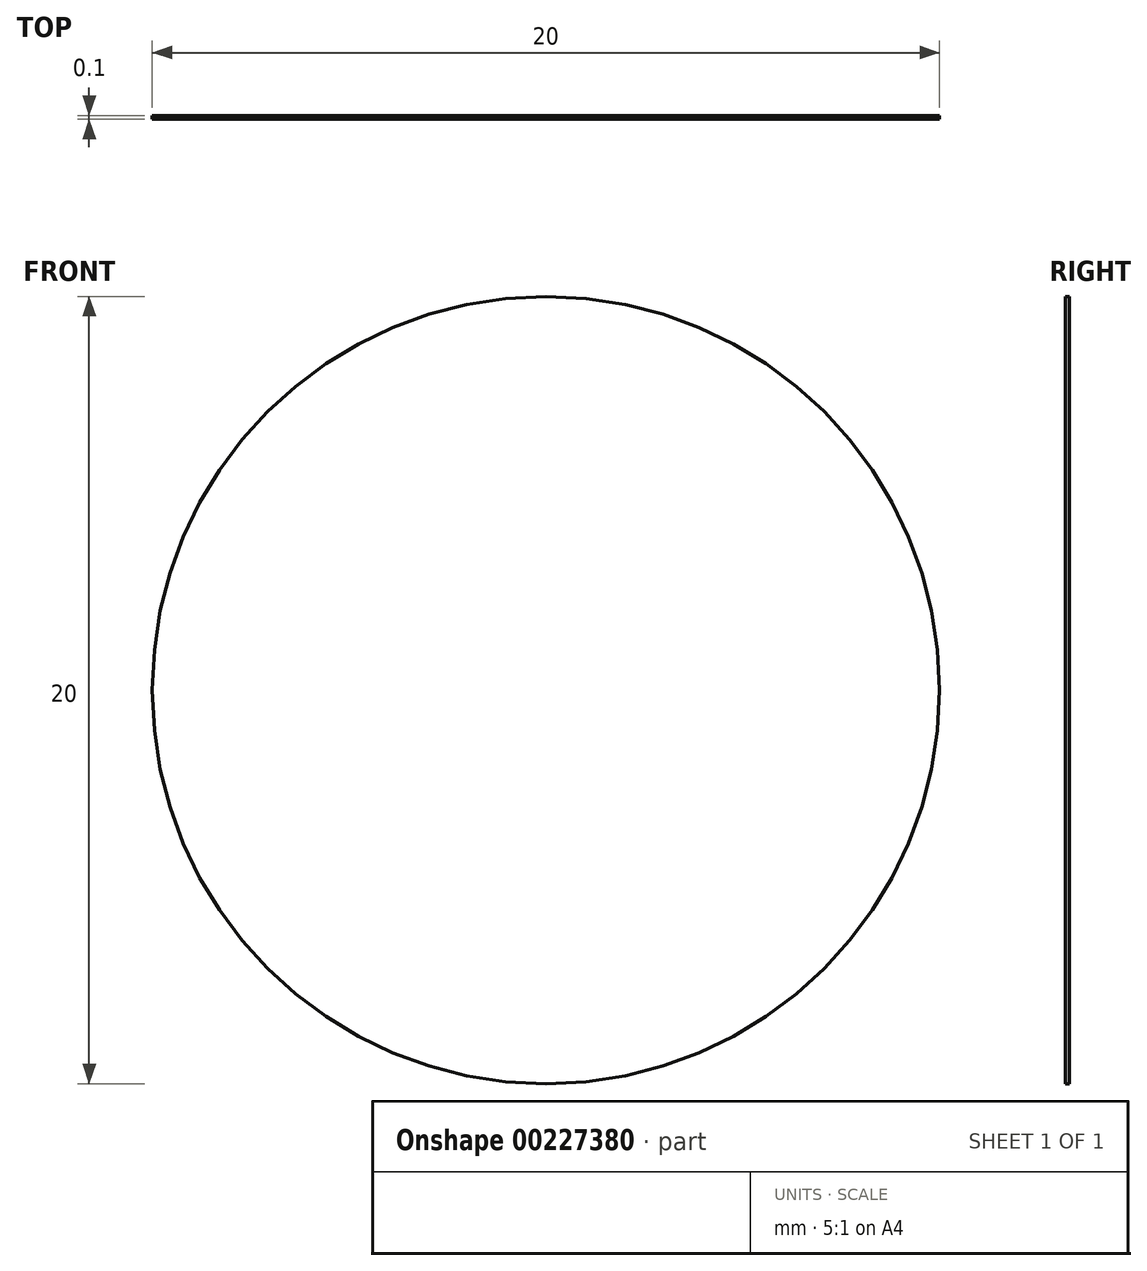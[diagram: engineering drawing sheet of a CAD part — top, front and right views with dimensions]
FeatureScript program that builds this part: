
annotation { "Feature Type Name" : "Feature", "Feature Type Description" : "" }
export const myFeature = defineFeature(function(context is Context, id is Id, definition is map)
    precondition{}
    {
        {
            var Q0;
            Q0=qCreatedBy(makeId("Front.planeOp"),FACE);
            var sketch = newSketch(context, id + "F0", { "sketchPlane" : qUnion([Q0])});
            skCircle(sketch, "E0", {"center": v(0, 0) * mm, "radius": 10 * mm});
            skSolve(sketch);
        }
        {
            var Q0;
            Q0=makeQuery(id+"F0.imprint","IMPRINT",FACE,{"disambiguationData":[TD([[makeQuery(id+"F0.imprint","IMPRINT",EDGE,{"derivedFrom":sQuery(id+"F0.wireOp",EDGE,"E0")}),1.0]])]});
            extrude(context, id + "F1", {"entities" : qUnion([Q0]), "depth" : 0.1 * mm});
        }
    });
